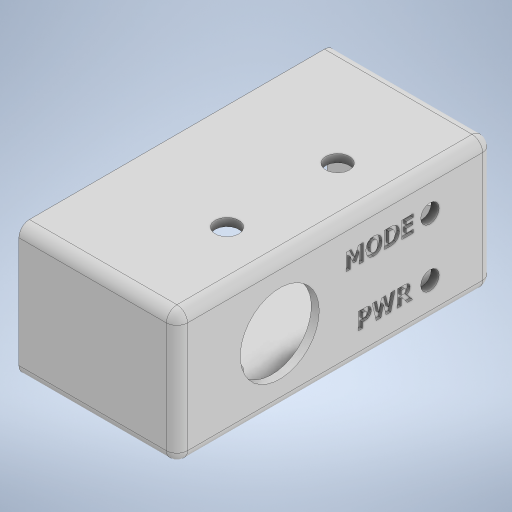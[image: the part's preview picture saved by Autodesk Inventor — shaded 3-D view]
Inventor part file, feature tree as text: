
AUTODESK INVENTOR PART (.ipt)
format: ipt  version: 2024.2 (Build 282272000, 272)  size: 418,816 bytes
history: native  units: mm
features: sketch x6, hole x3, extrude x2, shell x1, fillet x1, emboss x1
ambient origin geometry x8: Origin, YZ Plane, XZ Plane, XY Plane, X Axis, Y Axis, Z Axis, Center Point
bodies: Solid1 (feature_tree)
feature tree (14):
  extrude  "Extrusion1"  Depth=30.0mm
  shell  "Shell2"  Thickness=25.0mm
  extrude  "Extrusion2"  Depth=25.0mm TaperAngle=0.0deg
  hole  "Hole1"  [1 undecoded]
  fillet  "Fillet1"  Radius=10.5mm
  hole  "Hole2"  [1 undecoded]
  hole  "Hole3"  [1 undecoded]
  emboss  "Emboss1"
  sketch  "Sketch1"  dims[d0=30.0mm d1=60.0mm d2=25.0mm d3=0.0mm]
  sketch  "Sketch2"  dims[d5=1.5mm d7=25.0mm d8=0.0mm]
  sketch  "Sketch3"  dims[d9=21.0mm d10=10.0mm d11=10.5mm]
  sketch  "Sketch4"  dims[d12=4.5mm d13=6.0mm d14=4.0mm d15=2.0mm d16=90.0deg d17=9.0mm d18=20.594885mm d19=2.0mm]
  sketch  "Sketch5"  dims[d20=15.0mm d21=18.0mm]
  sketch  "Sketch6"  dims[d22=5.0mm d23=5.0mm d24=10.0mm d25=3.5mm d26=6.0mm d27=4.0mm d28=2.0mm d29=90.0deg d30=8.0mm d31=20.594885mm d32=10.0mm d33=8.0mm d34=6.0mm d35=4.0mm d36=2.0mm d37=90.0deg d38=8.0mm d39=20.594885mm d40=0.5mm d41=0.0mm]
note: 3 required parameter values undecoded (feature->parameter linkage not recoverable at this tier; creation-order binding heuristic only, values carry confidence <= 0.55)
